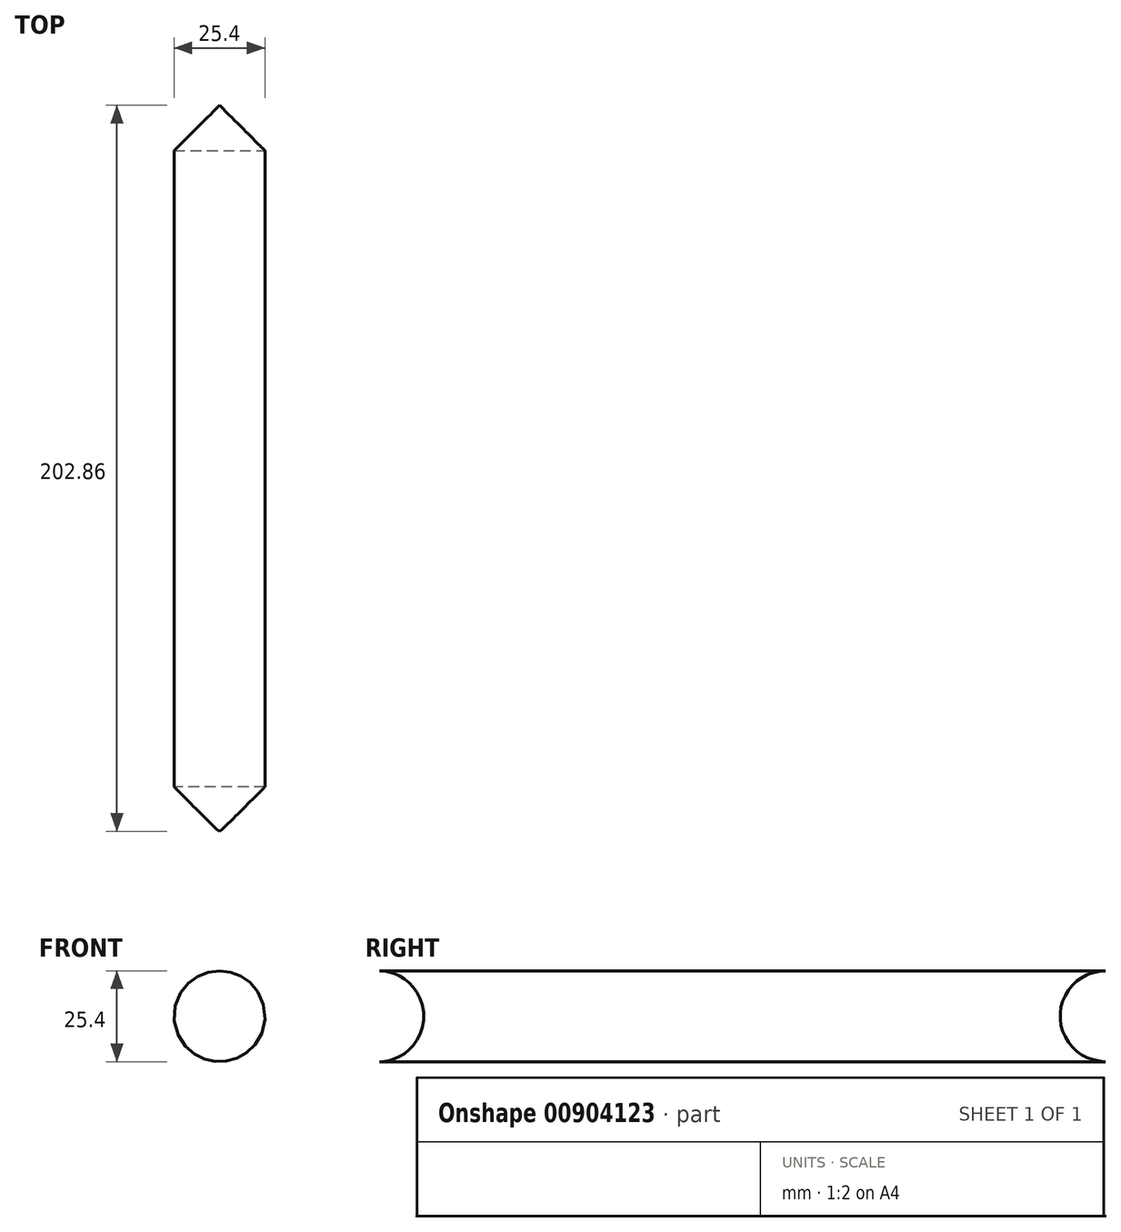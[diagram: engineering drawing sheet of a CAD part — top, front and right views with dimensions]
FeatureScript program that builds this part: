
annotation { "Feature Type Name" : "Feature", "Feature Type Description" : "" }
export const myFeature = defineFeature(function(context is Context, id is Id, definition is map)
    precondition{}
    {
        {
            var Q0;
            Q0=qCreatedBy(makeId("Front.planeOp"),FACE);
            var sketch = newSketch(context, id + "F0", { "sketchPlane" : qUnion([Q0])});
            skCircle(sketch, "E0", {"center": v(0, 0) * mm, "radius": 12.7 * mm});
            skSolve(sketch);
        }
        {
            var Q0;
            Q0=makeQuery(id+"F0.imprint","IMPRINT",FACE,{"disambiguationData":[TD([[makeQuery(id+"F0.imprint","IMPRINT",EDGE,{"derivedFrom":sQuery(id+"F0.wireOp",EDGE,"E0")}),1.0]])]});
            extrude(context, id + "F1", {"entities" : qUnion([Q0]), "depth" : 203.2 * mm, "offsetDistance" : 25.4 * mm});
        }
        {
            var Q0;
            Q0=makeQuery(id+"F1.opExtrude","CAP_FACE",FACE,{"disambiguationData":[OSD([sQuery(id+"F0.wireOp",EDGE,"E0")])],"isStart":false});
            var sketch = newSketch(context, id + "F2", { "sketchPlane" : qUnion([Q0])});
            skLineSegment(sketch, "E1.bottom", {"start": v(12.7, 12.7) * mm, "end": v(-12.7, 12.7) * mm});
            skLineSegment(sketch, "E1.top", {"start": v(12.7, -12.7) * mm, "end": v(-12.7, -12.7) * mm});
            skLineSegment(sketch, "E1.left", {"start": v(12.7, 12.7) * mm, "end": v(12.7, -12.7) * mm});
            skLineSegment(sketch, "E1.right", {"start": v(-12.7, 12.7) * mm, "end": v(-12.7, -12.7) * mm});
            skPoint(sketch, "E1.middle", {"position": v(0, 0) * mm});
            skSolve(sketch);
        }
        {
            var Q0;
            Q0=sQuery(id+"F2.wireOp",EDGE,"E1.right");
            cPlane(context, id + "F3", {"entities" : qUnion([Q0]), "cplaneType" : CPlaneType.LINE_ANGLE, "offset" : 25.4 * mm, "angle" : 0 * degree, "width" : 152.4 * mm, "height" : 152.4 * mm});
        }
        {
            var Q0;
            Q0=qCreatedBy(id+"F3.planeOp",FACE);
            var sketch = newSketch(context, id + "F4", { "sketchPlane" : qUnion([Q0])});
            skCircle(sketch, "E2", {"center": v(203.18, 0) * mm, "radius": 12.7 * mm});
            skSolve(sketch);
        }
        {
            var Q0;
            Q0=makeQuery(id+"F4.imprint","IMPRINT",FACE,{"disambiguationData":[TD([[makeQuery(id+"F4.imprint","IMPRINT",EDGE,{"derivedFrom":sQuery(id+"F4.wireOp",EDGE,"E2")}),1.0]])]});
            extrude(context, id + "F5", {"entities" : qUnion([Q0]), "operationType" : NewBodyOperationType.REMOVE, "oppositeDirection" : true, "depth" : 25.4 * mm, "offsetDistance" : 25.4 * mm});
        }
        {
            var Q0;
            Q0=makeQuery(id+"F1.opExtrude","CAP_FACE",FACE,{"disambiguationData":[OSD([sQuery(id+"F0.wireOp",EDGE,"E0")])],"isStart":true});
            var sketch = newSketch(context, id + "F6", { "sketchPlane" : qUnion([Q0])});
            skLineSegment(sketch, "E3.bottom", {"start": v(12.7, 12.7) * mm, "end": v(-12.7, 12.7) * mm});
            skLineSegment(sketch, "E3.top", {"start": v(12.7, -12.7) * mm, "end": v(-12.7, -12.7) * mm});
            skLineSegment(sketch, "E3.left", {"start": v(12.7, 12.7) * mm, "end": v(12.7, -12.7) * mm});
            skLineSegment(sketch, "E3.right", {"start": v(-12.7, 12.7) * mm, "end": v(-12.7, -12.7) * mm});
            skPoint(sketch, "E3.middle", {"position": v(0, 0) * mm});
            skSolve(sketch);
        }
        {
            var Q0;
            Q0=sQuery(id+"F6.wireOp",EDGE,"E3.right");
            cPlane(context, id + "F7", {"entities" : qUnion([Q0]), "cplaneType" : CPlaneType.LINE_ANGLE, "offset" : 25.4 * mm, "angle" : 0 * degree, "width" : 152.4 * mm, "height" : 152.4 * mm});
        }
        {
            var Q0;
            Q0=qCreatedBy(id+"F7.planeOp",FACE);
            var sketch = newSketch(context, id + "F8", { "sketchPlane" : qUnion([Q0])});
            skCircle(sketch, "E4", {"center": v(0, 0) * mm, "radius": 12.7 * mm});
            skSolve(sketch);
        }
        {
            var Q0;
            Q0=makeQuery(id+"F8.imprint","IMPRINT",FACE,{"disambiguationData":[TD([[makeQuery(id+"F8.imprint","IMPRINT",EDGE,{"derivedFrom":sQuery(id+"F8.wireOp",EDGE,"E4")}),1.0]])]});
            extrude(context, id + "F9", {"entities" : qUnion([Q0]), "operationType" : NewBodyOperationType.REMOVE, "depth" : 25.4 * mm, "offsetDistance" : 25.4 * mm});
        }
    });
